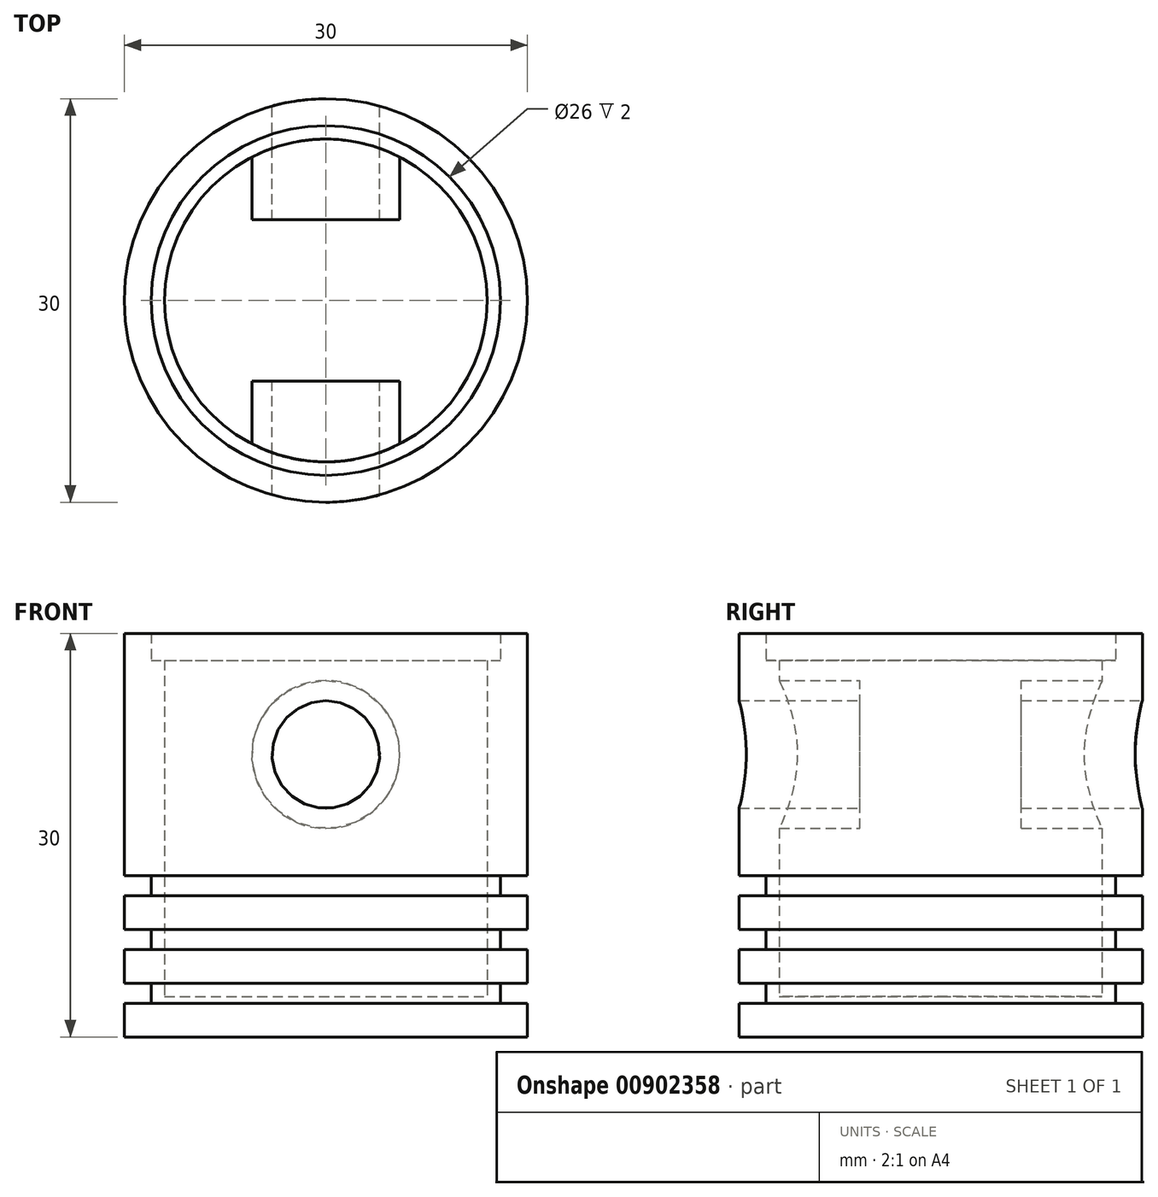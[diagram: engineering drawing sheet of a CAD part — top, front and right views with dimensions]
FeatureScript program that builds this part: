
annotation { "Feature Type Name" : "Feature", "Feature Type Description" : "" }
export const myFeature = defineFeature(function(context is Context, id is Id, definition is map)
    precondition{}
    {
        {
            var Q0;
            Q0=qCreatedBy(makeId("Front.planeOp"),FACE);
            var sketch = newSketch(context, id + "F0", { "sketchPlane" : qUnion([Q0])});
            skLineSegment(sketch, "E0", {"start": v(0, 0) * mm, "end": v(-15, 0) * mm});
            skLineSegment(sketch, "E1", {"start": v(-15, 0) * mm, "end": v(-15, 2.5) * mm});
            skLineSegment(sketch, "E2", {"start": v(-15, 2.5) * mm, "end": v(-13, 2.5) * mm});
            skLineSegment(sketch, "E3", {"start": v(-13, 2.5) * mm, "end": v(-13, 4) * mm});
            skLineSegment(sketch, "E4", {"start": v(-13, 4) * mm, "end": v(-15, 4) * mm});
            skLineSegment(sketch, "E5", {"start": v(-15, 4) * mm, "end": v(-15, 6.5) * mm});
            skLineSegment(sketch, "E6", {"start": v(-15, 6.5) * mm, "end": v(-13, 6.5) * mm});
            skLineSegment(sketch, "E7", {"start": v(-13, 6.5) * mm, "end": v(-13, 8) * mm});
            skLineSegment(sketch, "E8", {"start": v(-13, 8) * mm, "end": v(-15, 8) * mm});
            skLineSegment(sketch, "E9", {"start": v(-15, 8) * mm, "end": v(-15, 10.5) * mm});
            skLineSegment(sketch, "E10", {"start": v(-15, 10.5) * mm, "end": v(-13, 10.5) * mm});
            skLineSegment(sketch, "E11", {"start": v(-13, 10.5) * mm, "end": v(-13, 12) * mm});
            skLineSegment(sketch, "E12", {"start": v(-13, 12) * mm, "end": v(-15, 12) * mm});
            skLineSegment(sketch, "E13", {"start": v(-15, 12) * mm, "end": v(-15, 30) * mm});
            skLineSegment(sketch, "E14", {"start": v(-15, 30) * mm, "end": v(-13, 30) * mm});
            skLineSegment(sketch, "E15", {"start": v(-13, 30) * mm, "end": v(-13, 28) * mm});
            skLineSegment(sketch, "E16", {"start": v(-13, 28) * mm, "end": v(-12, 28) * mm});
            skLineSegment(sketch, "E17", {"start": v(-12, 28) * mm, "end": v(-12, 8) * mm});
            skLineSegment(sketch, "E18", {"start": v(-12, 8) * mm, "end": v(-12, 3) * mm});
            skLineSegment(sketch, "E19", {"start": v(-12, 3) * mm, "end": v(0, 3) * mm});
            skLineSegment(sketch, "E20", {"start": v(0, 0) * mm, "end": v(0, 3) * mm});
            skSolve(sketch);
        }
        {
            var Q0;
            Q0=makeQuery(id+"F0.imprint","IMPRINT",FACE,{"disambiguationData":[TD([[makeQuery(id+"F0.imprint","IMPRINT",EDGE,{"derivedFrom":sQuery(id+"F0.wireOp",EDGE,"E0")}),-1.0]])]});
            var Q1;
            Q1=sQuery(id+"F0.wireOp",EDGE,"E20");
            revolve(context, id + "F1", {"surfaceOperationType" : NewSurfaceOperationType.NEW, "entities" : qUnion([Q0]), "axis" : qUnion([Q1]), "revolveType" : RevolveType.FULL});
        }
        {
            var Q0;
            Q0=qCreatedBy(makeId("Front.planeOp"),FACE);
            var sketch = newSketch(context, id + "F2", { "sketchPlane" : qUnion([Q0])});
            skLineSegment(sketch, "E21", {"start": v(0, 0) * mm, "end": v(0, 12) * mm});
            skLineSegment(sketch, "E22", {"start": v(0, 12) * mm, "end": v(0, 21) * mm});
            skCircle(sketch, "E23", {"center": v(0, 21) * mm, "radius": 4 * mm});
            skCircle(sketch, "E24", {"center": v(0, 21) * mm, "radius": 5.5 * mm});
            skSolve(sketch);
        }
        {
            var Q0;
            Q0=makeQuery(id+"F2.imprint","IMPRINT",FACE,{"disambiguationData":[TD([[makeQuery(id+"F2.imprint","IMPRINT",EDGE,{"derivedFrom":sQuery(id+"F2.wireOp",EDGE,"E23")}),1.0]])]});
            extrude(context, id + "F3", {"entities" : qUnion([Q0]), "operationType" : NewBodyOperationType.REMOVE, "endBound" : BoundingType.SYMMETRIC, "depth" : 40 * mm, "offsetDistance" : 25 * mm});
        }
        {
            var Q0;
            Q0=makeQuery(id+"F2.imprint","IMPRINT",FACE,{"disambiguationData":[TD([[makeQuery(id+"F2.imprint","IMPRINT",EDGE,{"derivedFrom":sQuery(id+"F2.wireOp",EDGE,"E23")}),-1.0]])]});
            extrude(context, id + "F4", {"entities" : qUnion([Q0]), "operationType" : NewBodyOperationType.ADD, "endBound" : BoundingType.SYMMETRIC, "depth" : 24 * mm, "offsetDistance" : 25 * mm});
        }
        {
            var Q0;
            Q0 = qSketchRegion(id + "F2", true);
            extrude(context, id + "F5", {"entities" : qUnion([Q0]), "operationType" : NewBodyOperationType.REMOVE, "endBound" : BoundingType.SYMMETRIC, "oppositeDirection" : true, "depth" : 12 * mm, "offsetDistance" : 25 * mm});
        }
    });
